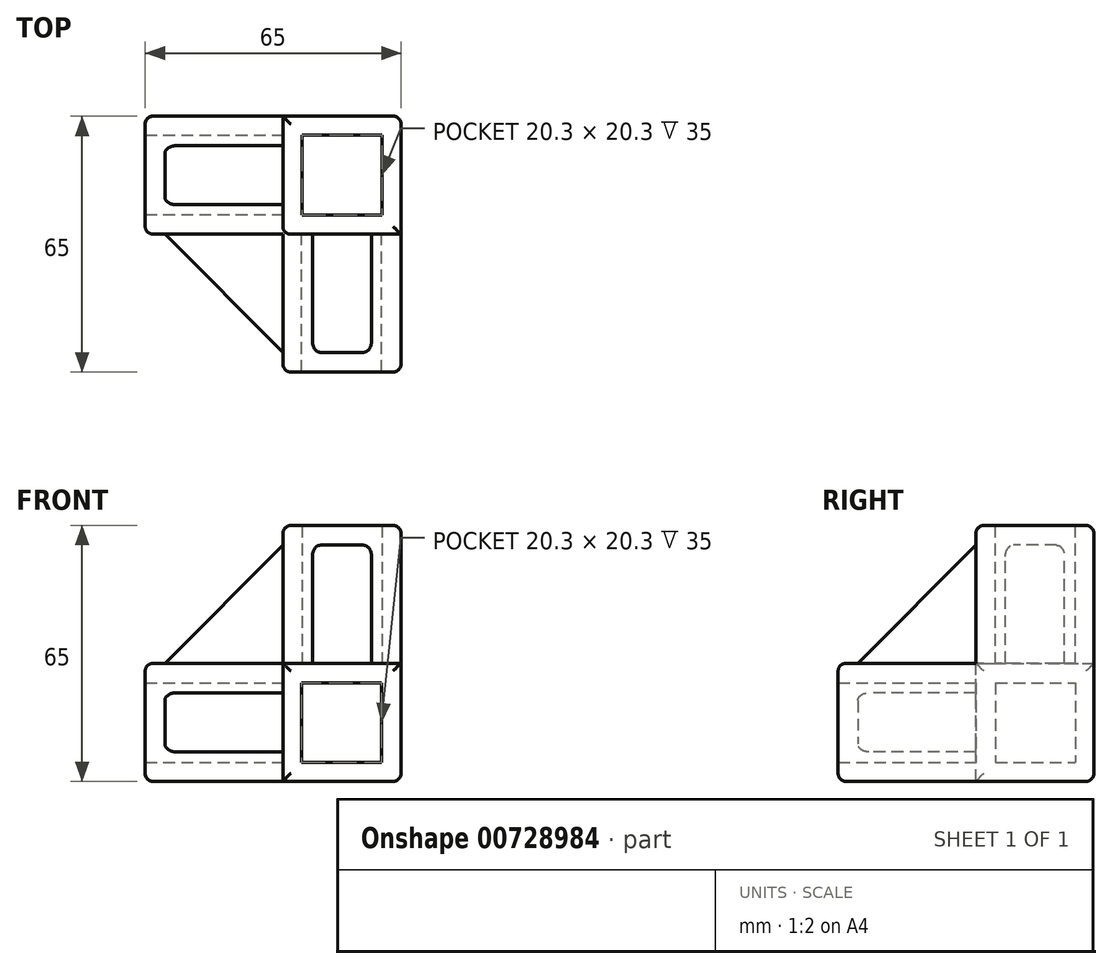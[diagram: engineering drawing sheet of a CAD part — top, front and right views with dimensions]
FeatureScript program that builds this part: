
annotation { "Feature Type Name" : "Feature", "Feature Type Description" : "" }
export const myFeature = defineFeature(function(context is Context, id is Id, definition is map)
    precondition{}
    {
        {
            var Q0;
            Q0=qCreatedBy(makeId("Front.planeOp"),FACE);
            var sketch = newSketch(context, id + "F0", { "sketchPlane" : qUnion([Q0])});
            skLineSegment(sketch, "E0.bottom", {"start": v(0, 0) * mm, "end": v(30, 0) * mm});
            skLineSegment(sketch, "E0.top", {"start": v(0, 30) * mm, "end": v(30, 30) * mm});
            skLineSegment(sketch, "E0.left", {"start": v(0, 0) * mm, "end": v(0, 30) * mm});
            skLineSegment(sketch, "E0.right", {"start": v(30, 0) * mm, "end": v(30, 30) * mm});
            skSolve(sketch);
        }
        {
            var Q0;
            Q0=makeQuery(id+"F0.imprint","IMPRINT",FACE,{"disambiguationData":[TD([[makeQuery(id+"F0.imprint","IMPRINT",EDGE,{"derivedFrom":sQuery(id+"F0.wireOp",EDGE,"E0.bottom")}),1.0]])]});
            extrude(context, id + "F1", {"entities" : qUnion([Q0]), "depth" : 30 * mm, "offsetDistance" : 25 * mm});
        }
        {
            var Q0;
            Q0=makeQuery(id+"F1.opExtrude","CAP_FACE",FACE,{"disambiguationData":[OSD([sQuery(id+"F0.wireOp",EDGE,"E0.bottom"),sQuery(id+"F0.wireOp",EDGE,"E0.top"),sQuery(id+"F0.wireOp",EDGE,"E0.left"),sQuery(id+"F0.wireOp",EDGE,"E0.right")])],"isStart":false});
            var sketch = newSketch(context, id + "F2", { "sketchPlane" : qUnion([Q0])});
            skLineSegment(sketch, "E1.bottom", {"start": v(25.05, 25.05) * mm, "end": v(4.75, 25.05) * mm});
            skLineSegment(sketch, "E1.top", {"start": v(25.05, 4.75) * mm, "end": v(4.75, 4.75) * mm});
            skLineSegment(sketch, "E1.left", {"start": v(25.05, 25.05) * mm, "end": v(25.05, 4.75) * mm});
            skLineSegment(sketch, "E1.right", {"start": v(4.75, 25.05) * mm, "end": v(4.75, 4.75) * mm});
            skPoint(sketch, "E1.middle", {"position": v(14.9, 14.9) * mm});
            skLineSegment(sketch, "E2.bottom", {"start": v(0, 0) * mm, "end": v(30, 0) * mm});
            skLineSegment(sketch, "E2.top", {"start": v(0, 30) * mm, "end": v(30, 30) * mm});
            skLineSegment(sketch, "E2.left", {"start": v(0, 0) * mm, "end": v(0, 30) * mm});
            skLineSegment(sketch, "E2.right", {"start": v(30, 0) * mm, "end": v(30, 30) * mm});
            skSolve(sketch);
        }
        {
            var Q0;
            Q0=makeQuery(id+"F2.imprint","IMPRINT",FACE,{"disambiguationData":[TD([[makeQuery(id+"F2.imprint","IMPRINT",EDGE,{"derivedFrom":sQuery(id+"F2.wireOp",EDGE,"E1.bottom")}),-1.0]])]});
            extrude(context, id + "F3", {"entities" : qUnion([Q0]), "operationType" : NewBodyOperationType.ADD, "depth" : 35 * mm, "offsetDistance" : 25 * mm});
        }
        {
            var Q0;
            Q0=makeQuery(id+"F3.boolean.opBoolean","MERGE",FACE,{"derivedFrom":[makeQuery(id+"F1.opExtrude","SWEPT_FACE",FACE,{"disambiguationData":[OSD([sQuery(id+"F0.wireOp",EDGE,"E0.left")])]}),makeQuery(id+"F3.opExtrude","SWEPT_FACE",FACE,{"disambiguationData":[OSD([sQuery(id+"F2.wireOp",EDGE,"E2.left")])]})]});
            var sketch = newSketch(context, id + "F4", { "sketchPlane" : qUnion([Q0])});
            skLineSegment(sketch, "E3.bottom", {"start": v(0, 0) * mm, "end": v(30, 0) * mm});
            skLineSegment(sketch, "E3.top", {"start": v(0, 30) * mm, "end": v(30, 30) * mm});
            skLineSegment(sketch, "E3.left", {"start": v(0, 0) * mm, "end": v(0, 30) * mm});
            skLineSegment(sketch, "E3.right", {"start": v(30, 0) * mm, "end": v(30, 30) * mm});
            skLineSegment(sketch, "E4.bottom", {"start": v(25.05, 25.05) * mm, "end": v(4.75, 25.05) * mm});
            skLineSegment(sketch, "E4.top", {"start": v(25.05, 4.75) * mm, "end": v(4.75, 4.75) * mm});
            skLineSegment(sketch, "E4.left", {"start": v(25.05, 25.05) * mm, "end": v(25.05, 4.75) * mm});
            skLineSegment(sketch, "E4.right", {"start": v(4.75, 25.05) * mm, "end": v(4.75, 4.75) * mm});
            skPoint(sketch, "E4.middle", {"position": v(14.9, 14.9) * mm});
            skSolve(sketch);
        }
        {
            var Q0;
            Q0=makeQuery(id+"F4.imprint","IMPRINT",FACE,{"disambiguationData":[TD([[makeQuery(id+"F4.imprint","IMPRINT",EDGE,{"derivedFrom":sQuery(id+"F4.wireOp",EDGE,"E3.bottom")}),-1.0]])]});
            extrude(context, id + "F5", {"entities" : qUnion([Q0]), "operationType" : NewBodyOperationType.ADD, "depth" : 35 * mm, "offsetDistance" : 25 * mm});
        }
        {
            var Q0;
            Q0=makeQuery(id+"F5.boolean.opBoolean","MERGE",FACE,{"derivedFrom":[makeQuery(id+"F3.boolean.opBoolean","MERGE",FACE,{"derivedFrom":[makeQuery(id+"F1.opExtrude","SWEPT_FACE",FACE,{"disambiguationData":[OSD([sQuery(id+"F0.wireOp",EDGE,"E0.top")])]}),makeQuery(id+"F3.opExtrude","SWEPT_FACE",FACE,{"disambiguationData":[OSD([sQuery(id+"F2.wireOp",EDGE,"E2.top")])]})]}),makeQuery(id+"F5.opExtrude","SWEPT_FACE",FACE,{"disambiguationData":[OSD([sQuery(id+"F4.wireOp",EDGE,"E3.top")])]})]});
            var sketch = newSketch(context, id + "F6", { "sketchPlane" : qUnion([Q0])});
            skLineSegment(sketch, "E5.bottom", {"start": v(30, 0) * mm, "end": v(0, 0) * mm});
            skLineSegment(sketch, "E5.top", {"start": v(30, -30) * mm, "end": v(0, -30) * mm});
            skLineSegment(sketch, "E5.left", {"start": v(30, 0) * mm, "end": v(30, -30) * mm});
            skLineSegment(sketch, "E5.right", {"start": v(0, 0) * mm, "end": v(0, -30) * mm});
            skLineSegment(sketch, "E6.bottom", {"start": v(25.15, -4.85) * mm, "end": v(4.85, -4.85) * mm});
            skLineSegment(sketch, "E6.top", {"start": v(25.15, -25.15) * mm, "end": v(4.85, -25.15) * mm});
            skLineSegment(sketch, "E6.left", {"start": v(25.15, -4.85) * mm, "end": v(25.15, -25.15) * mm});
            skLineSegment(sketch, "E6.right", {"start": v(4.85, -4.85) * mm, "end": v(4.85, -25.15) * mm});
            skPoint(sketch, "E6.middle", {"position": v(15, -15) * mm});
            skPoint(sketch, "E6.middle.positionSnap0", {"position": v(0, -15) * mm});
            skPoint(sketch, "E6.middle.positionSnap1", {"position": v(15, -30) * mm});
            skPoint(sketch, "E6.centerSnap0", {"position": v(0, -15) * mm});
            skPoint(sketch, "E6.centerSnap1", {"position": v(15, -30) * mm});
            skSolve(sketch);
        }
        {
            var Q0;
            Q0=makeQuery(id+"F6.imprint","IMPRINT",FACE,{"disambiguationData":[TD([[makeQuery(id+"F6.imprint","IMPRINT",EDGE,{"derivedFrom":sQuery(id+"F6.wireOp",EDGE,"E5.bottom")}),-1.0]])]});
            extrude(context, id + "F7", {"entities" : qUnion([Q0]), "operationType" : NewBodyOperationType.ADD, "depth" : 35 * mm, "offsetDistance" : 25 * mm});
        }
        {
            var Q0;
            Q0=makeQuery(id+"F5.opExtrude","SWEPT_FACE",FACE,{"disambiguationData":[OSD([sQuery(id+"F4.wireOp",EDGE,"E3.right")])]});
            var sketch = newSketch(context, id + "F8", { "sketchPlane" : qUnion([Q0])});
            skLineSegment(sketch, "E7", {"start": v(0, 30) * mm, "end": v(0, 60) * mm});
            skLineSegment(sketch, "E8", {"start": v(0, 30) * mm, "end": v(-30, 30) * mm});
            skLineSegment(sketch, "E9", {"start": v(-30, 30) * mm, "end": v(0, 60) * mm});
            skSolve(sketch);
        }
        {
            var Q0;
            Q0=makeQuery(id+"F8.imprint","IMPRINT",FACE,{"disambiguationData":[TD([[makeQuery(id+"F8.imprint","IMPRINT",EDGE,{"derivedFrom":sQuery(id+"F8.wireOp",EDGE,"E7")}),1.0]])]});
            extrude(context, id + "F9", {"entities" : qUnion([Q0]), "operationType" : NewBodyOperationType.ADD, "oppositeDirection" : true, "depth" : 30 * mm, "offsetDistance" : 25 * mm});
        }
        {
            var Q0;
            Q0=makeQuery(id+"F5.opExtrude","CAP_FACE",FACE,{"disambiguationData":[OSD([sQuery(id+"F4.wireOp",EDGE,"E3.bottom"),sQuery(id+"F4.wireOp",EDGE,"E3.top"),sQuery(id+"F4.wireOp",EDGE,"E3.left"),sQuery(id+"F4.wireOp",EDGE,"E3.right"),sQuery(id+"F4.wireOp",EDGE,"E4.bottom"),sQuery(id+"F4.wireOp",EDGE,"E4.top"),sQuery(id+"F4.wireOp",EDGE,"E4.left"),sQuery(id+"F4.wireOp",EDGE,"E4.right")])],"isStart":false});
            var sketch = newSketch(context, id + "F10", { "sketchPlane" : qUnion([Q0])});
            skLineSegment(sketch, "E10", {"start": v(15, 30) * mm, "end": v(22.5, 30) * mm});
            skLineSegment(sketch, "E11.bottom", {"start": v(22.5, 30) * mm, "end": v(7.5, 30) * mm});
            skLineSegment(sketch, "E11.top", {"start": v(22.5, 60) * mm, "end": v(7.5, 60) * mm});
            skLineSegment(sketch, "E11.left", {"start": v(22.5, 30) * mm, "end": v(22.5, 60) * mm});
            skLineSegment(sketch, "E11.right", {"start": v(7.5, 30) * mm, "end": v(7.5, 60) * mm});
            skLineSegment(sketch, "E12.bottom", {"start": v(0, 30) * mm, "end": v(30, 30) * mm});
            skLineSegment(sketch, "E12.top", {"start": v(0, 60) * mm, "end": v(30, 60) * mm});
            skLineSegment(sketch, "E12.left", {"start": v(0, 30) * mm, "end": v(0, 60) * mm});
            skLineSegment(sketch, "E12.right", {"start": v(30, 30) * mm, "end": v(30, 60) * mm});
            skSolve(sketch);
        }
        {
            var Q0;
            {var subQ0=sQuery(id+"F10.wireOp",EDGE,"E11.right");Q0=makeQuery(id+"F10.imprint","IMPRINT",FACE,{"disambiguationData":[TD([[makeQuery(id+"F10.imprint","IMPRINT",EDGE,{"derivedFrom":subQ0}),1.0]])]});}
            var Q1;
            {var subQ0=sQuery(id+"F10.wireOp",EDGE,"E11.left");Q1=makeQuery(id+"F10.imprint","IMPRINT",FACE,{"disambiguationData":[TD([[makeQuery(id+"F10.imprint","IMPRINT",EDGE,{"derivedFrom":subQ0}),-1.0]])]});}
            extrude(context, id + "F11", {"entities" : qUnion([Q0, Q1]), "operationType" : NewBodyOperationType.REMOVE, "oppositeDirection" : true, "depth" : 35 * mm, "offsetDistance" : 25 * mm});
        }
        {
            var Q0;
            {var subQ1=sQuery(id+"F2.wireOp",EDGE,"E2.left");Q0=makeQuery(id+"F5.boolean.opBoolean","SPLIT",FACE,{"disambiguationData":[TD([makeQuery(id+"F1.opExtrude","SWEPT_FACE",FACE,{"disambiguationData":[OSD([sQuery(id+"F0.wireOp",EDGE,"E0.bottom")])]})])],"derivedFrom":makeQuery(id+"F3.boolean.opBoolean","MERGE",FACE,{"derivedFrom":[makeQuery(id+"F1.opExtrude","SWEPT_FACE",FACE,{"disambiguationData":[OSD([sQuery(id+"F0.wireOp",EDGE,"E0.left")])]}),makeQuery(id+"F3.opExtrude","SWEPT_FACE",FACE,{"disambiguationData":[OSD([subQ1])]})]})});}
            var sketch = newSketch(context, id + "F12", { "sketchPlane" : qUnion([Q0])});
            skLineSegment(sketch, "E13", {"start": v(30, 30) * mm, "end": v(30, 60) * mm});
            skLineSegment(sketch, "E14", {"start": v(30, 30) * mm, "end": v(60, 30) * mm});
            skLineSegment(sketch, "E15", {"start": v(60, 30) * mm, "end": v(30, 60) * mm});
            skSolve(sketch);
        }
        {
            var Q0;
            Q0=makeQuery(id+"F12.imprint","IMPRINT",FACE,{"disambiguationData":[TD([[makeQuery(id+"F12.imprint","IMPRINT",EDGE,{"derivedFrom":sQuery(id+"F12.wireOp",EDGE,"E13")}),-1.0]])]});
            extrude(context, id + "F13", {"entities" : qUnion([Q0]), "operationType" : NewBodyOperationType.ADD, "oppositeDirection" : true, "depth" : 30 * mm, "offsetDistance" : 25 * mm});
        }
        {
            var Q0;
            Q0=makeQuery(id+"F3.opExtrude","CAP_FACE",FACE,{"disambiguationData":[OSD([sQuery(id+"F2.wireOp",EDGE,"E1.bottom"),sQuery(id+"F2.wireOp",EDGE,"E1.top"),sQuery(id+"F2.wireOp",EDGE,"E1.left"),sQuery(id+"F2.wireOp",EDGE,"E1.right"),sQuery(id+"F2.wireOp",EDGE,"E2.bottom"),sQuery(id+"F2.wireOp",EDGE,"E2.top"),sQuery(id+"F2.wireOp",EDGE,"E2.left"),sQuery(id+"F2.wireOp",EDGE,"E2.right")])],"isStart":false});
            var sketch = newSketch(context, id + "F14", { "sketchPlane" : qUnion([Q0])});
            skLineSegment(sketch, "E16", {"start": v(15, 30) * mm, "end": v(22.5, 30) * mm});
            skLineSegment(sketch, "E17.bottom", {"start": v(0, 30) * mm, "end": v(30, 30) * mm});
            skLineSegment(sketch, "E17.top", {"start": v(0, 65) * mm, "end": v(30, 65) * mm});
            skLineSegment(sketch, "E17.left", {"start": v(0, 30) * mm, "end": v(0, 65) * mm});
            skLineSegment(sketch, "E17.right", {"start": v(30, 30) * mm, "end": v(30, 65) * mm});
            skLineSegment(sketch, "E18.bottom", {"start": v(22.5, 30) * mm, "end": v(7.5, 30) * mm});
            skLineSegment(sketch, "E18.top", {"start": v(22.5, 60) * mm, "end": v(7.5, 60) * mm});
            skLineSegment(sketch, "E18.left", {"start": v(22.5, 30) * mm, "end": v(22.5, 60) * mm});
            skLineSegment(sketch, "E18.right", {"start": v(7.5, 30) * mm, "end": v(7.5, 60) * mm});
            skSolve(sketch);
        }
        {
            var Q0;
            Q0=makeQuery(id+"F14.imprint","IMPRINT",FACE,{"disambiguationData":[TD([[makeQuery(id+"F14.imprint","IMPRINT",EDGE,{"derivedFrom":sQuery(id+"F14.wireOp",EDGE,"E17.top")}),-1.0]])]});
            extrude(context, id + "F15", {"entities" : qUnion([Q0]), "operationType" : NewBodyOperationType.REMOVE, "oppositeDirection" : true, "depth" : 35 * mm, "offsetDistance" : 25 * mm});
        }
        {
            var Q0;
            Q0=makeQuery(id+"F5.boolean.opBoolean","MERGE",FACE,{"derivedFrom":[makeQuery(id+"F3.boolean.opBoolean","MERGE",FACE,{"derivedFrom":[makeQuery(id+"F1.opExtrude","SWEPT_FACE",FACE,{"disambiguationData":[OSD([sQuery(id+"F0.wireOp",EDGE,"E0.bottom")])]}),makeQuery(id+"F3.opExtrude","SWEPT_FACE",FACE,{"disambiguationData":[OSD([sQuery(id+"F2.wireOp",EDGE,"E2.bottom")])]})]}),makeQuery(id+"F5.opExtrude","SWEPT_FACE",FACE,{"disambiguationData":[OSD([sQuery(id+"F4.wireOp",EDGE,"E3.bottom")])]})]});
            var sketch = newSketch(context, id + "F16", { "sketchPlane" : qUnion([Q0])});
            skLineSegment(sketch, "E19.bottom", {"start": v(0, 30) * mm, "end": v(-30, 30) * mm});
            skLineSegment(sketch, "E19.top", {"start": v(0, 60) * mm, "end": v(-30, 60) * mm});
            skLineSegment(sketch, "E19.left", {"start": v(0, 30) * mm, "end": v(0, 60) * mm});
            skLineSegment(sketch, "E19.right", {"start": v(-30, 30) * mm, "end": v(-30, 60) * mm});
            skLineSegment(sketch, "E20", {"start": v(-30, 30) * mm, "end": v(0, 60) * mm});
            skSolve(sketch);
        }
        {
            var Q0;
            Q0=makeQuery(id+"F16.imprint","IMPRINT",FACE,{"disambiguationData":[TD([[makeQuery(id+"F16.imprint","IMPRINT",EDGE,{"derivedFrom":sQuery(id+"F16.wireOp",EDGE,"E19.bottom")}),1.0]])]});
            extrude(context, id + "F17", {"entities" : qUnion([Q0]), "operationType" : NewBodyOperationType.ADD, "oppositeDirection" : true, "depth" : 30 * mm, "offsetDistance" : 25 * mm});
        }
        {
            var Q0;
            Q0=makeQuery(id+"F5.opExtrude","CAP_FACE",FACE,{"disambiguationData":[OSD([sQuery(id+"F4.wireOp",EDGE,"E3.bottom"),sQuery(id+"F4.wireOp",EDGE,"E3.top"),sQuery(id+"F4.wireOp",EDGE,"E3.left"),sQuery(id+"F4.wireOp",EDGE,"E3.right"),sQuery(id+"F4.wireOp",EDGE,"E4.bottom"),sQuery(id+"F4.wireOp",EDGE,"E4.top"),sQuery(id+"F4.wireOp",EDGE,"E4.left"),sQuery(id+"F4.wireOp",EDGE,"E4.right")])],"isStart":false});
            var sketch = newSketch(context, id + "F18", { "sketchPlane" : qUnion([Q0])});
            skLineSegment(sketch, "E21.bottom", {"start": v(30, 30) * mm, "end": v(65, 30) * mm});
            skLineSegment(sketch, "E21.top", {"start": v(30, 0) * mm, "end": v(65, 0) * mm});
            skLineSegment(sketch, "E21.left", {"start": v(30, 30) * mm, "end": v(30, 0) * mm});
            skLineSegment(sketch, "E21.right", {"start": v(65, 30) * mm, "end": v(65, 0) * mm});
            skLineSegment(sketch, "E22", {"start": v(30, 15) * mm, "end": v(30, 22.5) * mm});
            skLineSegment(sketch, "E23.bottom", {"start": v(30, 22.5) * mm, "end": v(65, 22.5) * mm});
            skLineSegment(sketch, "E23.top", {"start": v(30, 7.5) * mm, "end": v(65, 7.5) * mm});
            skLineSegment(sketch, "E23.left", {"start": v(30, 22.5) * mm, "end": v(30, 7.5) * mm});
            skLineSegment(sketch, "E23.right", {"start": v(65, 22.5) * mm, "end": v(65, 7.5) * mm});
            skSolve(sketch);
        }
        {
            var Q0;
            {var subQ0=sQuery(id+"F18.wireOp",EDGE,"E21.bottom");Q0=makeQuery(id+"F18.imprint","IMPRINT",FACE,{"disambiguationData":[TD([[makeQuery(id+"F18.imprint","IMPRINT",EDGE,{"derivedFrom":subQ0}),-1.0]])]});}
            var Q1;
            {var subQ0=sQuery(id+"F18.wireOp",EDGE,"E21.top");Q1=makeQuery(id+"F18.imprint","IMPRINT",FACE,{"disambiguationData":[TD([[makeQuery(id+"F18.imprint","IMPRINT",EDGE,{"derivedFrom":subQ0}),1.0]])]});}
            extrude(context, id + "F19", {"entities" : qUnion([Q0, Q1]), "operationType" : NewBodyOperationType.REMOVE, "oppositeDirection" : true, "depth" : 35 * mm, "offsetDistance" : 25 * mm});
        }
        {
            var Q0;
            Q0=makeQuery(id+"F5.opExtrude","CAP_EDGE",EDGE,{"disambiguationData":[OSD([sQuery(id+"F4.wireOp",EDGE,"E3.top")])],"isStart":false});
            var Q1;
            Q1=makeQuery(id+"F5.opExtrude","CAP_EDGE",EDGE,{"disambiguationData":[OSD([sQuery(id+"F4.wireOp",EDGE,"E3.right")])],"isStart":false});
            var Q2;
            Q2=makeQuery(id+"F5.opExtrude","CAP_EDGE",EDGE,{"disambiguationData":[OSD([sQuery(id+"F4.wireOp",EDGE,"E3.bottom")])],"isStart":false});
            var Q3;
            Q3=makeQuery(id+"F5.opExtrude","CAP_EDGE",EDGE,{"disambiguationData":[OSD([sQuery(id+"F4.wireOp",EDGE,"E3.left")])],"isStart":false});
            var Q4;
            Q4=makeQuery(id+"F3.opExtrude","CAP_EDGE",EDGE,{"disambiguationData":[OSD([sQuery(id+"F2.wireOp",EDGE,"E2.left")])],"isStart":false});
            var Q5;
            Q5=makeQuery(id+"F3.opExtrude","CAP_EDGE",EDGE,{"disambiguationData":[OSD([sQuery(id+"F2.wireOp",EDGE,"E2.top")])],"isStart":false});
            var Q6;
            Q6=makeQuery(id+"F3.opExtrude","CAP_EDGE",EDGE,{"disambiguationData":[OSD([sQuery(id+"F2.wireOp",EDGE,"E2.right")])],"isStart":false});
            var Q7;
            Q7=makeQuery(id+"F3.opExtrude","CAP_EDGE",EDGE,{"disambiguationData":[OSD([sQuery(id+"F2.wireOp",EDGE,"E2.bottom")])],"isStart":false});
            var Q8;
            Q8=makeQuery(id+"F7.opExtrude","CAP_EDGE",EDGE,{"disambiguationData":[OSD([sQuery(id+"F6.wireOp",EDGE,"E5.left")])],"isStart":false});
            var Q9;
            Q9=makeQuery(id+"F7.opExtrude","CAP_EDGE",EDGE,{"disambiguationData":[OSD([sQuery(id+"F6.wireOp",EDGE,"E5.bottom")])],"isStart":false});
            var Q10;
            Q10=makeQuery(id+"F7.opExtrude","CAP_EDGE",EDGE,{"disambiguationData":[OSD([sQuery(id+"F6.wireOp",EDGE,"E5.right")])],"isStart":false});
            var Q11;
            Q11=makeQuery(id+"F7.opExtrude","CAP_EDGE",EDGE,{"disambiguationData":[OSD([sQuery(id+"F6.wireOp",EDGE,"E5.top")])],"isStart":false});
            var Q12;
            Q12=makeQuery(id+"F15.boolean.opBoolean","INTERSECT",EDGE,{"derivedFrom":[makeQuery(id+"F13.opExtrude","SWEPT_FACE",FACE,{"disambiguationData":[OSD([sQuery(id+"F12.wireOp",EDGE,"E15")])]}),makeQuery(id+"F15.opExtrude","SWEPT_FACE",FACE,{"disambiguationData":[OSD([sQuery(id+"F14.wireOp",EDGE,"E18.right")])]})]});
            var Q13;
            Q13=makeQuery(id+"F15.boolean.opBoolean","INTERSECT",EDGE,{"derivedFrom":[makeQuery(id+"F13.opExtrude","SWEPT_FACE",FACE,{"disambiguationData":[OSD([sQuery(id+"F12.wireOp",EDGE,"E15")])]}),makeQuery(id+"F15.opExtrude","SWEPT_FACE",FACE,{"disambiguationData":[OSD([sQuery(id+"F14.wireOp",EDGE,"E18.left")])]})]});
            var Q14;
            Q14=makeQuery(id+"F11.boolean.opBoolean","INTERSECT",EDGE,{"derivedFrom":[makeQuery(id+"F9.opExtrude","SWEPT_FACE",FACE,{"disambiguationData":[OSD([sQuery(id+"F8.wireOp",EDGE,"E9")])]}),makeQuery(id+"F11.opExtrude","SWEPT_FACE",FACE,{"disambiguationData":[OSD([sQuery(id+"F10.wireOp",EDGE,"E11.left")])]})]});
            var Q15;
            Q15=makeQuery(id+"F11.boolean.opBoolean","INTERSECT",EDGE,{"derivedFrom":[makeQuery(id+"F9.opExtrude","SWEPT_FACE",FACE,{"disambiguationData":[OSD([sQuery(id+"F8.wireOp",EDGE,"E9")])]}),makeQuery(id+"F11.opExtrude","SWEPT_FACE",FACE,{"disambiguationData":[OSD([sQuery(id+"F10.wireOp",EDGE,"E11.right")])]})]});
            var Q16;
            Q16=makeQuery(id+"F19.boolean.opBoolean","INTERSECT",EDGE,{"derivedFrom":[makeQuery(id+"F17.opExtrude","SWEPT_FACE",FACE,{"disambiguationData":[OSD([sQuery(id+"F16.wireOp",EDGE,"E20")])]}),makeQuery(id+"F19.opExtrude","SWEPT_FACE",FACE,{"disambiguationData":[OSD([sQuery(id+"F18.wireOp",EDGE,"E23.bottom")])]})]});
            var Q17;
            Q17=makeQuery(id+"F19.boolean.opBoolean","INTERSECT",EDGE,{"derivedFrom":[makeQuery(id+"F17.opExtrude","SWEPT_FACE",FACE,{"disambiguationData":[OSD([sQuery(id+"F16.wireOp",EDGE,"E20")])]}),makeQuery(id+"F19.opExtrude","SWEPT_FACE",FACE,{"disambiguationData":[OSD([sQuery(id+"F18.wireOp",EDGE,"E23.top")])]})]});
            var Q18;
            Q18=makeQuery(id+"F7.boolean.opBoolean","MERGE",EDGE,{"derivedFrom":[makeQuery(id+"F1.opExtrude","CAP_EDGE",EDGE,{"disambiguationData":[OSD([sQuery(id+"F0.wireOp",EDGE,"E0.right")])],"isStart":true}),makeQuery(id+"F7.opExtrude","SWEPT_EDGE",EDGE,{"disambiguationData":[OSD([sQuery(id+"F6.wireOp",EDGE,"E5.bottom"),sQuery(id+"F6.wireOp",EDGE,"E5.left")])]})]});
            var Q19;
            Q19=makeQuery(id+"F3.boolean.opBoolean","MERGE",EDGE,{"derivedFrom":[makeQuery(id+"F1.opExtrude","SWEPT_EDGE",EDGE,{"disambiguationData":[OSD([sQuery(id+"F0.wireOp",EDGE,"E0.bottom"),sQuery(id+"F0.wireOp",EDGE,"E0.right")])]}),makeQuery(id+"F3.opExtrude","SWEPT_EDGE",EDGE,{"disambiguationData":[OSD([sQuery(id+"F2.wireOp",EDGE,"E2.bottom"),sQuery(id+"F2.wireOp",EDGE,"E2.right")])]})]});
            var Q20;
            {var subQ0=sQuery(id+"F2.wireOp",EDGE,"E2.right");Q20=makeQuery(id+"F15.boolean.opBoolean","MERGE",EDGE,{"derivedFrom":[makeQuery(id+"F3.boolean.opBoolean","MERGE",EDGE,{"derivedFrom":[makeQuery(id+"F1.opExtrude","SWEPT_EDGE",EDGE,{"disambiguationData":[OSD([sQuery(id+"F0.wireOp",EDGE,"E0.top"),sQuery(id+"F0.wireOp",EDGE,"E0.right")])]}),makeQuery(id+"F3.opExtrude","SWEPT_EDGE",EDGE,{"disambiguationData":[OSD([sQuery(id+"F2.wireOp",EDGE,"E2.top"),subQ0])]})]}),makeQuery(id+"F15.opExtrude","SWEPT_EDGE",EDGE,{"disambiguationData":[OSD([subQ0,sQuery(id+"F14.wireOp",EDGE,"E17.bottom"),sQuery(id+"F14.wireOp",EDGE,"E17.right")])]})]});}
            var Q21;
            Q21=makeQuery(id+"F15.boolean.opBoolean","MERGE",EDGE,{"derivedFrom":[makeQuery(id+"F7.opExtrude","SWEPT_EDGE",EDGE,{"disambiguationData":[OSD([sQuery(id+"F0.wireOp",EDGE,"E0.top"),sQuery(id+"F0.wireOp",EDGE,"E0.right"),sQuery(id+"F2.wireOp",EDGE,"E2.top"),sQuery(id+"F2.wireOp",EDGE,"E2.right"),sQuery(id+"F6.wireOp",EDGE,"E5.top"),sQuery(id+"F6.wireOp",EDGE,"E5.left")])]}),makeQuery(id+"F15.opExtrude","CAP_EDGE",EDGE,{"disambiguationData":[OSD([sQuery(id+"F14.wireOp",EDGE,"E17.right")])],"isStart":false})]});
            var Q22;
            Q22=makeQuery(id+"F19.boolean.opBoolean","MERGE",EDGE,{"derivedFrom":[makeQuery(id+"F3.boolean.opBoolean","MERGE",EDGE,{"derivedFrom":[makeQuery(id+"F1.opExtrude","SWEPT_EDGE",EDGE,{"disambiguationData":[OSD([sQuery(id+"F0.wireOp",EDGE,"E0.bottom"),sQuery(id+"F0.wireOp",EDGE,"E0.left")])]}),makeQuery(id+"F3.opExtrude","SWEPT_EDGE",EDGE,{"disambiguationData":[OSD([sQuery(id+"F2.wireOp",EDGE,"E2.bottom"),sQuery(id+"F2.wireOp",EDGE,"E2.left")])]})]}),makeQuery(id+"F19.opExtrude","CAP_EDGE",EDGE,{"disambiguationData":[OSD([sQuery(id+"F18.wireOp",EDGE,"E21.top")])],"isStart":false})]});
            var Q23;
            {var subQ0=sQuery(id+"F4.wireOp",EDGE,"E3.bottom");Q23=makeQuery(id+"F19.boolean.opBoolean","MERGE",EDGE,{"derivedFrom":[makeQuery(id+"F5.opExtrude","SWEPT_EDGE",EDGE,{"disambiguationData":[OSD([sQuery(id+"F0.wireOp",EDGE,"E0.bottom"),sQuery(id+"F0.wireOp",EDGE,"E0.left"),sQuery(id+"F2.wireOp",EDGE,"E2.bottom"),sQuery(id+"F2.wireOp",EDGE,"E2.left"),subQ0,sQuery(id+"F4.wireOp",EDGE,"E3.right")])]}),makeQuery(id+"F19.opExtrude","SWEPT_EDGE",EDGE,{"disambiguationData":[OSD([subQ0,sQuery(id+"F18.wireOp",EDGE,"E21.top"),sQuery(id+"F18.wireOp",EDGE,"E21.left")])]})]});}
            var Q24;
            Q24=makeQuery(id+"F5.boolean.opBoolean","MERGE",EDGE,{"derivedFrom":[makeQuery(id+"F1.opExtrude","CAP_EDGE",EDGE,{"disambiguationData":[OSD([sQuery(id+"F0.wireOp",EDGE,"E0.bottom")])],"isStart":true}),makeQuery(id+"F5.opExtrude","SWEPT_EDGE",EDGE,{"disambiguationData":[OSD([sQuery(id+"F4.wireOp",EDGE,"E3.bottom"),sQuery(id+"F4.wireOp",EDGE,"E3.left")])]})]});
            var Q25;
            {var subQ0=sQuery(id+"F4.wireOp",EDGE,"E3.left");Q25=makeQuery(id+"F11.boolean.opBoolean","MERGE",EDGE,{"derivedFrom":[makeQuery(id+"F5.boolean.opBoolean","MERGE",EDGE,{"derivedFrom":[makeQuery(id+"F1.opExtrude","CAP_EDGE",EDGE,{"disambiguationData":[OSD([sQuery(id+"F0.wireOp",EDGE,"E0.top")])],"isStart":true}),makeQuery(id+"F5.opExtrude","SWEPT_EDGE",EDGE,{"disambiguationData":[OSD([sQuery(id+"F4.wireOp",EDGE,"E3.top"),subQ0])]})]}),makeQuery(id+"F11.opExtrude","SWEPT_EDGE",EDGE,{"disambiguationData":[OSD([subQ0,sQuery(id+"F10.wireOp",EDGE,"E12.bottom"),sQuery(id+"F10.wireOp",EDGE,"E12.left")])]})]});}
            var Q26;
            Q26=makeQuery(id+"F11.boolean.opBoolean","MERGE",EDGE,{"derivedFrom":[makeQuery(id+"F7.opExtrude","SWEPT_EDGE",EDGE,{"disambiguationData":[OSD([sQuery(id+"F0.wireOp",EDGE,"E0.top"),sQuery(id+"F4.wireOp",EDGE,"E3.top"),sQuery(id+"F4.wireOp",EDGE,"E3.left"),sQuery(id+"F6.wireOp",EDGE,"E5.bottom"),sQuery(id+"F6.wireOp",EDGE,"E5.right")])]}),makeQuery(id+"F11.opExtrude","CAP_EDGE",EDGE,{"disambiguationData":[OSD([sQuery(id+"F10.wireOp",EDGE,"E12.left")])],"isStart":false})]});
            var Q27;
            {var subQ0=sQuery(id+"F4.wireOp",EDGE,"E3.top");var subQ1=sQuery(id+"F4.wireOp",EDGE,"E3.right");Q27=makeQuery(id+"F19.boolean.opBoolean","MERGE",EDGE,{"derivedFrom":[makeQuery(id+"F11.boolean.opBoolean","MERGE",EDGE,{"derivedFrom":[makeQuery(id+"F5.opExtrude","SWEPT_EDGE",EDGE,{"disambiguationData":[OSD([sQuery(id+"F0.wireOp",EDGE,"E0.top"),sQuery(id+"F0.wireOp",EDGE,"E0.left"),sQuery(id+"F2.wireOp",EDGE,"E2.top"),sQuery(id+"F2.wireOp",EDGE,"E2.left"),subQ0,subQ1])]}),makeQuery(id+"F11.opExtrude","SWEPT_EDGE",EDGE,{"disambiguationData":[OSD([subQ1,sQuery(id+"F10.wireOp",EDGE,"E12.bottom"),sQuery(id+"F10.wireOp",EDGE,"E12.right")])]})]}),makeQuery(id+"F19.opExtrude","SWEPT_EDGE",EDGE,{"disambiguationData":[OSD([subQ0,sQuery(id+"F18.wireOp",EDGE,"E21.bottom"),sQuery(id+"F18.wireOp",EDGE,"E21.left")])]})]});}
            fillet(context, id + "F20", {"entities" : qUnion([Q0, Q1, Q2, Q3, Q4, Q5, Q6, Q7, Q8, Q9, Q10, Q11, Q12, Q13, Q14, Q15, Q16, Q17, Q18, Q19, Q20, Q21, Q22, Q23, Q24, Q25, Q26, Q27]), "radius" : 2 * mm, "tangentPropagation" : true, "allowEdgeOverflow" : false});
        }
        {
            var Q0;
            Q0=makeQuery(id+"F15.boolean.opBoolean","MERGE",EDGE,{"derivedFrom":[makeQuery(id+"F11.boolean.opBoolean","MERGE",EDGE,{"derivedFrom":[makeQuery(id+"F7.opExtrude","SWEPT_EDGE",EDGE,{"disambiguationData":[OSD([sQuery(id+"F0.wireOp",EDGE,"E0.top"),sQuery(id+"F0.wireOp",EDGE,"E0.left"),sQuery(id+"F2.wireOp",EDGE,"E2.top"),sQuery(id+"F2.wireOp",EDGE,"E2.left"),sQuery(id+"F4.wireOp",EDGE,"E3.top"),sQuery(id+"F4.wireOp",EDGE,"E3.right"),sQuery(id+"F6.wireOp",EDGE,"E5.top"),sQuery(id+"F6.wireOp",EDGE,"E5.right")])]}),makeQuery(id+"F11.opExtrude","CAP_EDGE",EDGE,{"disambiguationData":[OSD([sQuery(id+"F10.wireOp",EDGE,"E12.right")])],"isStart":false})]}),makeQuery(id+"F15.opExtrude","CAP_EDGE",EDGE,{"disambiguationData":[OSD([sQuery(id+"F14.wireOp",EDGE,"E17.left")])],"isStart":false})]});
            var Q1;
            {var subQ0=sQuery(id+"F2.wireOp",EDGE,"E2.left");Q1=makeQuery(id+"F19.boolean.opBoolean","MERGE",EDGE,{"derivedFrom":[makeQuery(id+"F15.boolean.opBoolean","MERGE",EDGE,{"derivedFrom":[makeQuery(id+"F3.boolean.opBoolean","MERGE",EDGE,{"derivedFrom":[makeQuery(id+"F1.opExtrude","SWEPT_EDGE",EDGE,{"disambiguationData":[OSD([sQuery(id+"F0.wireOp",EDGE,"E0.top"),sQuery(id+"F0.wireOp",EDGE,"E0.left")])]}),makeQuery(id+"F3.opExtrude","SWEPT_EDGE",EDGE,{"disambiguationData":[OSD([sQuery(id+"F2.wireOp",EDGE,"E2.top"),subQ0])]})]}),makeQuery(id+"F15.opExtrude","SWEPT_EDGE",EDGE,{"disambiguationData":[OSD([subQ0,sQuery(id+"F14.wireOp",EDGE,"E17.bottom"),sQuery(id+"F14.wireOp",EDGE,"E17.left")])]})]}),makeQuery(id+"F19.opExtrude","CAP_EDGE",EDGE,{"disambiguationData":[OSD([sQuery(id+"F18.wireOp",EDGE,"E21.bottom")])],"isStart":false})]});}
            fillet(context, id + "F21", {"entities" : qUnion([Q0, Q1]), "radius" : 2 * mm, "tangentPropagation" : true, "allowEdgeOverflow" : false});
        }
    });
